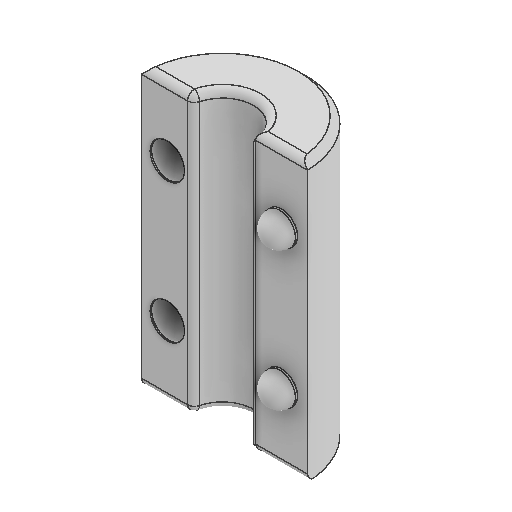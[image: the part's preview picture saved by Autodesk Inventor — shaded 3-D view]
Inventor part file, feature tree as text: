
AUTODESK INVENTOR PART (.ipt)
format: ipt  version: 2025 (Build 290162000, 162)  size: 220,672 bytes
history: native  units: mm
features: projected_geometry x5, fillet x4, sketch x4, extrude x3, thicken_offset x2, revolve x1, chamfer x1
ambient origin geometry x8: Origin, YZ Plane, XZ Plane, XY Plane, X Axis, Y Axis, Z Axis, Center Point
bodies: Solid1 (feature_tree)
feature tree (20):
  revolve  "Revolution1"  [1 undecoded]
  extrude  "Extrusion1"  TaperAngle=180.0deg  [1 undecoded]
  fillet  "Fillet1"  Radius=2.5mm
  extrude  "Extrusion2"  Depth=5.0mm
  fillet  "Fillet2"  Radius=5.0mm
  thicken_offset  "Thicken1"
  thicken_offset  "Thicken2"
  chamfer  "Chamfer1"  Distance=1.25mm
  extrude  "Extrusion3"  Depth=0.5mm
  fillet  "Fillet4"  Radius=1.5mm
  fillet  "Fillet5"  Radius=1.25mm
  sketch  "Sketch1"  dims[d0=2.25mm d1=6.0mm]
  sketch  "Sketch2"  dims[d2=20.0mm d3=180.0deg d5=2.5mm]
  projected_geometry  "Projected Loop1"
  sketch  "Sketch3"  dims[d6=2.5mm d7=5.0mm d8=5.0mm d9=1.25mm d10=0.0mm]
  projected_geometry  "Projected Loop2"
  projected_geometry  "Projected Loop3"
  sketch  "Sketch4"  dims[d11=1.25mm d12=2.5mm d13=1.5mm d14=0.0mm d15=1.25mm d16=0.1mm d17=0.1mm d18=0.1mm d19=0.1mm d21=0.5mm d22=2.0mm d23=45.0deg d24=0.15mm d25=0.0mm d26=0.5mm d27=0.5mm]
  projected_geometry  "Projected Loop4"
  projected_geometry  "Projected Loop5"
note: 2 required parameter values undecoded (feature->parameter linkage not recoverable at this tier; creation-order binding heuristic only, values carry confidence <= 0.55)